# Revit family: Mixer_Basin_Nero_BiancaCare
name_source: partatom
category: Plumbing Fixtures
units: mm (PartAtom-declared; Revit-internal decimal feet)

## family parameters
Always vertical = Yes
Cut with Voids When Loaded = Yes
Maintain Annotation Orientation = No
OmniClass Number = 23.31.00.00
OmniClass Title = Plumbing Specific Products and Equipment
Part Type = Normal
Room Calculation Point = No
Round Connector Dimension = Use Diameter
Shared = No
Work Plane-Based = No

## types (6) — shared parameters
Assembly Code = D2010
CW Connection = Yes
Default Elevation = 900 mm
HW Connection = Yes
IfcExportAs = IfcValveType
Manufacturer = Nero
ManufacturerOverallDepth = 184 mm
ManufacturerOverallHeight = 198 mm
ManufacturerOverallWidth = 50 mm  [stored 0.164042 ft]
ManufacturerURLProductSpecific = https://nerotapware.com.au
ModifiedIssue = 20251105 $
URL = https://nerotapware.com.au
Uniclass2015Code = Pr_40_20_87
Uniclass2015Title = Taps and water supply outlet fittings
Uniclass2015Version = Products v1.35
Vent Connection = No
Waste Connection = No
zero-valued in all types: CWFU, HWFU, WFU

## per-type parameters (varying)
| type | Description | IfcExportType | ManufacturerSpecCode | Material | Model | Type Comments |
| Chrome (NR321502aCH) | Bianca Care Basin Mixer Chrome | FAUCET | NR321502aCH | Metal_Chrome_Nero | NR321502aCH | Mixer - Basin - Chrome |
| Matte Black (NR321502aMB) | Bianca Care Basin Mixer Matte Black | NOTDEFINED | NR321502aMB | Metal_MatteBlack_Nero | NR321502aMB | Mixer - Basin - Matte Black |
| Brushed Nickel (NR321502aBN) | Bianca Care Basin Mixer Brushed Nickel | NOTDEFINED | NR321502aBN | Metal_Nickel_Nero_Brushed | NR321502aBN | Mixer - Basin - Brushed Nickel |
| Gunmetal (NR321502aGM) | Bianca Care Basin Mixer Gun Metal | NOTDEFINED | NR321502aGM | Metal_GunMetal_Nero | NR321502aGM | Mixer - Basin - Gunmetal |
| Brushed Gold (NR321502aBG) | Bianca Care Basin Mixer Brushed Gold | NOTDEFINED | NR321502aBG | Metal_Gold_Nero_Brushed | NR321502aBG | Mixer - Basin - Brushed Gold |
| Brushed Bronze (NR321502aBZ) | Bianca Care Basin Mixer Brushed Bronze | NOTDEFINED | NR321502aBZ | Metal_Bronze_Nero_Brushed | NR321502aBZ | Mixer - Basin - Brushed Bronze |

note: [stored X ft] marks values corroborated as IEEE doubles in the binary element streams (Revit-internal decimal feet)

## geometry (parser evidence)
native form markers: Sweep x2
no freeform markers — native parametric forms only
